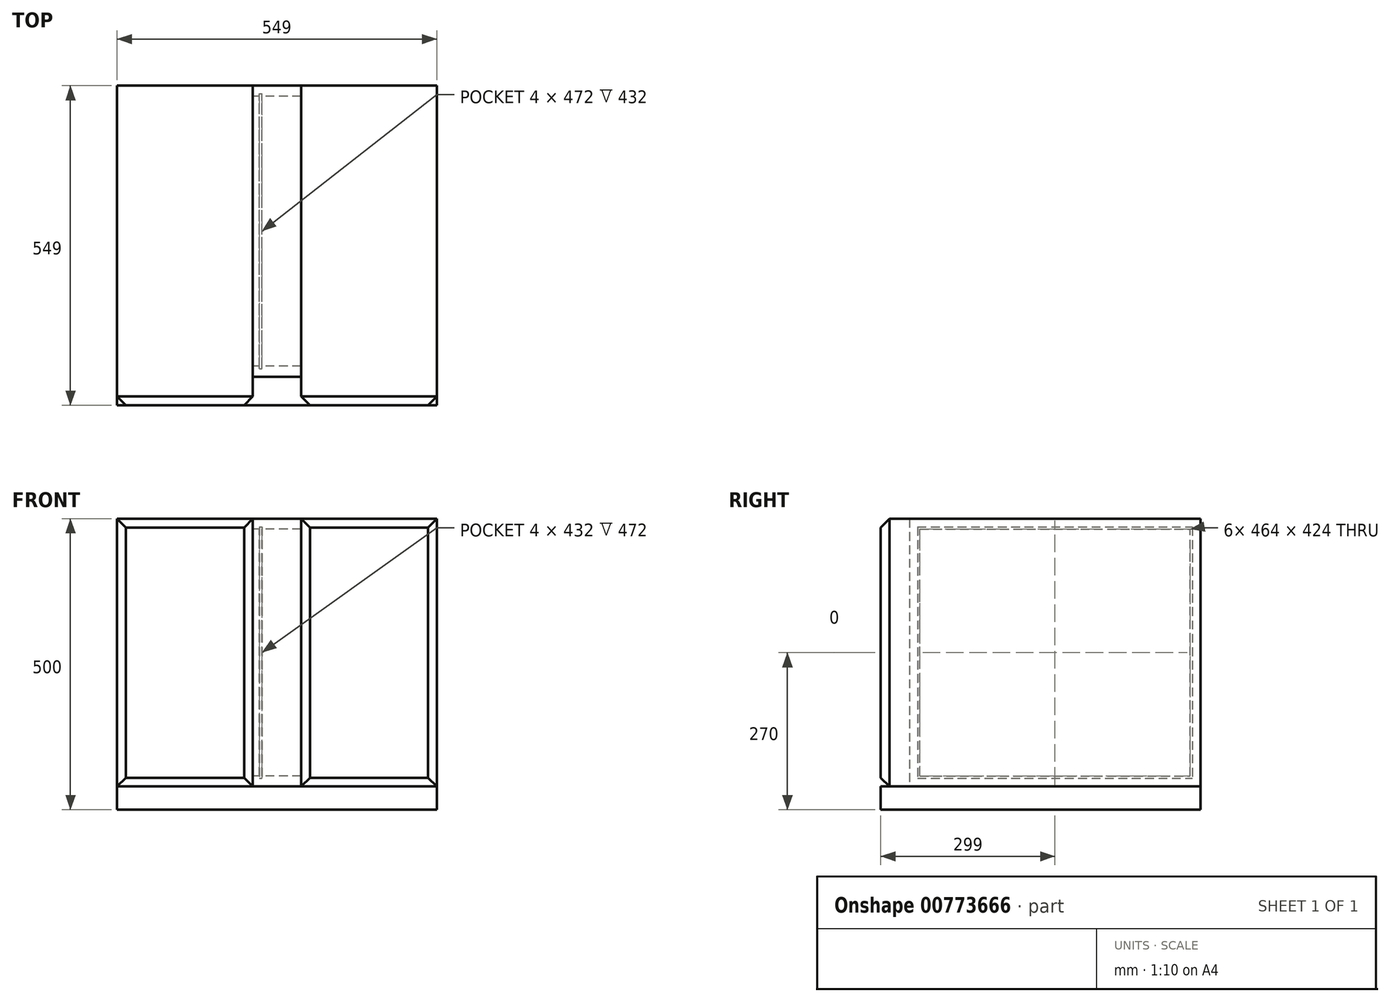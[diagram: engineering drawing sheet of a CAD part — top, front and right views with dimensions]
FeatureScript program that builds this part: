
annotation { "Feature Type Name" : "Feature", "Feature Type Description" : "" }
export const myFeature = defineFeature(function(context is Context, id is Id, definition is map)
    precondition{}
    {
        {
            var Q0;
            Q0=qCreatedBy(makeId("Top.planeOp"),FACE);
            var sketch = newSketch(context, id + "F0", { "sketchPlane" : qUnion([Q0])});
            skLineSegment(sketch, "E0.bottom", {"start": v(274.5, -274.5) * mm, "end": v(-274.5, -274.5) * mm});
            skLineSegment(sketch, "E0.top", {"start": v(274.5, 274.5) * mm, "end": v(-274.5, 274.5) * mm});
            skLineSegment(sketch, "E0.left", {"start": v(274.5, -274.5) * mm, "end": v(274.5, 274.5) * mm});
            skLineSegment(sketch, "E0.right", {"start": v(-274.5, -274.5) * mm, "end": v(-274.5, 274.5) * mm});
            skPoint(sketch, "E0.middle", {"position": v(0, 0) * mm});
            skSolve(sketch);
        }
        {
            var Q0;
            Q0 = qSketchRegion(id + "F0", true);
            extrude(context, id + "F1", {"entities" : qUnion([Q0]), "depth" : 40 * mm, "offsetDistance" : 25 * mm});
        }
        {
            var Q0;
            Q0=makeQuery(id+"F1.opExtrude","CAP_FACE",FACE,{"disambiguationData":[OSD([sQuery(id+"F0.wireOp",EDGE,"E0.bottom"),sQuery(id+"F0.wireOp",EDGE,"E0.top"),sQuery(id+"F0.wireOp",EDGE,"E0.left"),sQuery(id+"F0.wireOp",EDGE,"E0.right")])],"isStart":false});
            var sketch = newSketch(context, id + "F2", { "sketchPlane" : qUnion([Q0])});
            skLineSegment(sketch, "E1.bottom", {"start": v(-274.5, 274.5) * mm, "end": v(-41.5, 274.5) * mm});
            skLineSegment(sketch, "E1.top", {"start": v(-274.5, -274.5) * mm, "end": v(-41.5, -274.5) * mm});
            skLineSegment(sketch, "E1.left", {"start": v(-274.5, 274.5) * mm, "end": v(-274.5, -274.5) * mm});
            skLineSegment(sketch, "E1.right", {"start": v(-41.5, 274.5) * mm, "end": v(-41.5, -274.5) * mm});
            skLineSegment(sketch, "E2.bottom", {"start": v(274.5, 274.5) * mm, "end": v(41.5, 274.5) * mm});
            skLineSegment(sketch, "E2.top", {"start": v(274.5, -274.5) * mm, "end": v(41.5, -274.5) * mm});
            skLineSegment(sketch, "E2.left", {"start": v(274.5, 274.5) * mm, "end": v(274.5, -274.5) * mm});
            skLineSegment(sketch, "E2.right", {"start": v(41.5, 274.5) * mm, "end": v(41.5, -274.5) * mm});
            skSolve(sketch);
        }
        {
            var Q0;
            Q0=makeQuery(id+"F2.imprint","IMPRINT",FACE,{"disambiguationData":[TD([[makeQuery(id+"F2.imprint","IMPRINT",EDGE,{"derivedFrom":sQuery(id+"F2.wireOp",EDGE,"E1.bottom")}),1.0]])]});
            var Q1;
            Q1=makeQuery(id+"F2.imprint","IMPRINT",FACE,{"disambiguationData":[TD([[makeQuery(id+"F2.imprint","IMPRINT",EDGE,{"derivedFrom":sQuery(id+"F2.wireOp",EDGE,"E2.bottom")}),1.0]])]});
            extrude(context, id + "F3", {"entities" : qUnion([Q0, Q1]), "depth" : 460 * mm, "offsetDistance" : 25 * mm});
        }
        {
            var Q0;
            Q0=makeQuery(id+"F3.opExtrude","SWEPT_FACE",FACE,{"disambiguationData":[OSD([sQuery(id+"F2.wireOp",EDGE,"E2.top")])]});
            var Q1;
            Q1=makeQuery(id+"F3.opExtrude","SWEPT_FACE",FACE,{"disambiguationData":[OSD([sQuery(id+"F2.wireOp",EDGE,"E1.top")])]});
            chamfer(context, id + "F4", {"entities" : qUnion([Q0, Q1]), "width" : 15 * mm, "tangentPropagation" : true});
        }
        {
            var Q0;
            Q0=makeQuery(id+"F3.opExtrude","SWEPT_FACE",FACE,{"disambiguationData":[OSD([sQuery(id+"F2.wireOp",EDGE,"E1.right")])]});
            var sketch = newSketch(context, id + "F5", { "sketchPlane" : qUnion([Q0])});
            skLineSegment(sketch, "E3.bottom", {"start": v(274.5, 500) * mm, "end": v(-225.5, 500) * mm});
            skLineSegment(sketch, "E3.top", {"start": v(274.5, 40) * mm, "end": v(-225.5, 40) * mm});
            skLineSegment(sketch, "E3.left", {"start": v(274.5, 500) * mm, "end": v(274.5, 40) * mm});
            skLineSegment(sketch, "E3.right", {"start": v(-225.5, 500) * mm, "end": v(-225.5, 40) * mm});
            skLineSegment(sketch, "E4.bottom", {"start": v(-207.5, 58) * mm, "end": v(256.5, 58) * mm});
            skLineSegment(sketch, "E4.top", {"start": v(-207.5, 482) * mm, "end": v(256.5, 482) * mm});
            skLineSegment(sketch, "E4.left", {"start": v(-207.5, 58) * mm, "end": v(-207.5, 482) * mm});
            skLineSegment(sketch, "E4.right", {"start": v(256.5, 58) * mm, "end": v(256.5, 482) * mm});
            skSolve(sketch);
        }
        {
            var Q0;
            Q0 = qSketchRegion(id + "F5", true);
            var Q1;
            Q1=makeQuery(id+"F5.imprint","IMPRINT",FACE,{"disambiguationData":[TD([[makeQuery(id+"F5.imprint","IMPRINT",EDGE,{"derivedFrom":sQuery(id+"F5.wireOp",EDGE,"E3.bottom")}),1.0]])]});
            extrude(context, id + "F6", {"entities" : qUnion([Q0, Q1]), "depth" : 83 * mm, "offsetDistance" : 25 * mm});
        }
        {
            var Q0;
            Q0=qCreatedBy(makeId("Right.planeOp"),FACE);
            var sketch = newSketch(context, id + "F7", { "sketchPlane" : qUnion([Q0])});
            skLineSegment(sketch, "E5.bottom", {"start": v(-211.5, 486) * mm, "end": v(260.5, 486) * mm});
            skLineSegment(sketch, "E5.top", {"start": v(-211.5, 54) * mm, "end": v(260.5, 54) * mm});
            skLineSegment(sketch, "E5.left", {"start": v(-211.5, 486) * mm, "end": v(-211.5, 54) * mm});
            skLineSegment(sketch, "E5.right", {"start": v(260.5, 486) * mm, "end": v(260.5, 54) * mm});
            skSolve(sketch);
        }
        {
            var Q0;
            Q0=makeQuery(id+"F7.imprint","IMPRINT",FACE,{"disambiguationData":[TD([[makeQuery(id+"F7.imprint","IMPRINT",EDGE,{"derivedFrom":sQuery(id+"F7.wireOp",EDGE,"E5.bottom")}),-1.0]])]});
            extrude(context, id + "F8", {"entities" : qUnion([Q0]), "oppositeDirection" : true, "depth" : 30 * mm, "offsetDistance" : 25 * mm, "hasSecondDirection" : true, "secondDirectionOppositeDirection" : true, "secondDirectionDepth" : 26 * mm});
        }
        {
            var Q0;
            Q0=makeQuery(id+"F8.opExtrude","SWEPT_BODY",BODY,{"disambiguationData":[OSD([sQuery(id+"F7.wireOp",EDGE,"E5.bottom"),sQuery(id+"F7.wireOp",EDGE,"E5.top"),sQuery(id+"F7.wireOp",EDGE,"E5.left"),sQuery(id+"F7.wireOp",EDGE,"E5.right")])]});
            var Q1;
            Q1=makeQuery(id+"F6.opExtrude","SWEPT_BODY",BODY,{"disambiguationData":[OSD([sQuery(id+"F5.wireOp",EDGE,"E3.bottom"),sQuery(id+"F5.wireOp",EDGE,"E3.top"),sQuery(id+"F5.wireOp",EDGE,"E3.left"),sQuery(id+"F5.wireOp",EDGE,"E3.right"),sQuery(id+"F5.wireOp",EDGE,"E4.bottom"),sQuery(id+"F5.wireOp",EDGE,"E4.top"),sQuery(id+"F5.wireOp",EDGE,"E4.left"),sQuery(id+"F5.wireOp",EDGE,"E4.right")])]});
            booleanBodies(context, id + "F9", {"operationType" : BooleanOperationType.SUBTRACTION, "tools" : qUnion([Q0]), "targets" : qUnion([Q1]), "keepTools" : true});
        }
    });
